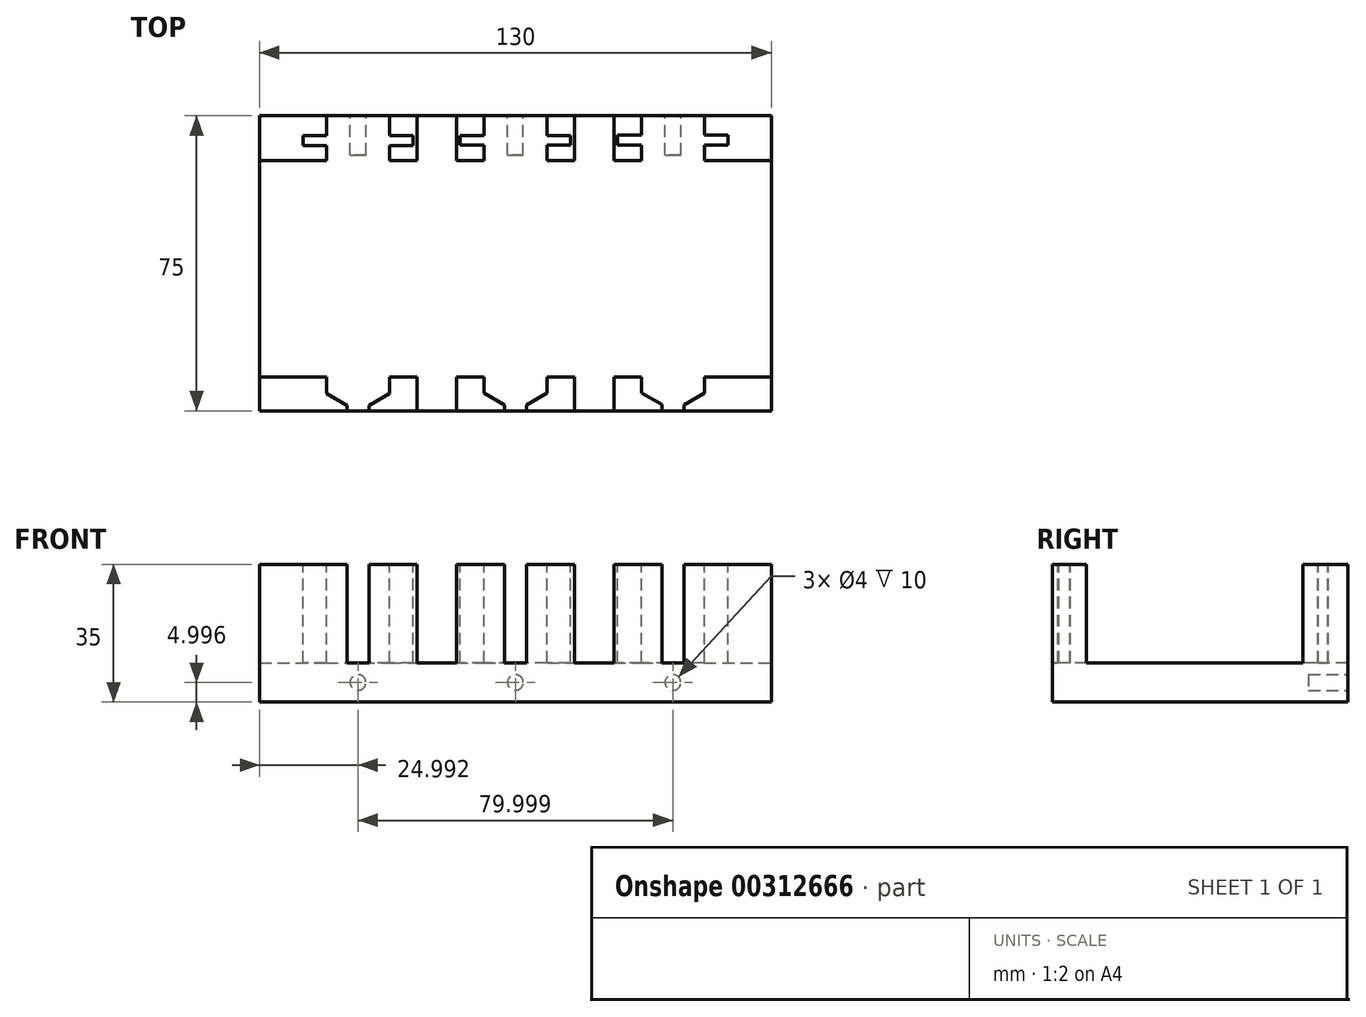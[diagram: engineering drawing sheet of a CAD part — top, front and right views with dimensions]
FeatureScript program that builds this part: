
annotation { "Feature Type Name" : "Feature", "Feature Type Description" : "" }
export const myFeature = defineFeature(function(context is Context, id is Id, definition is map)
    precondition{}
    {
        {
            var Q0;
            Q0=qCreatedBy(makeId("Front.planeOp"),FACE);
            var sketch = newSketch(context, id + "F0", { "sketchPlane" : qUnion([Q0])});
            skLineSegment(sketch, "E0.bottom", {"start": v(-64.2, 25.08) * mm, "end": v(65.8, 25.08) * mm});
            skLineSegment(sketch, "E0.top", {"start": v(-64.2, -24.92) * mm, "end": v(65.8, -24.92) * mm});
            skLineSegment(sketch, "E0.left", {"start": v(-64.2, 25.08) * mm, "end": v(-64.2, -24.92) * mm});
            skLineSegment(sketch, "E0.right", {"start": v(65.8, 25.08) * mm, "end": v(65.8, -24.92) * mm});
            skSolve(sketch);
        }
        {
            var Q0;
            Q0=makeQuery(id+"F0.imprint","IMPRINT",FACE,{"disambiguationData":[TD([[makeQuery(id+"F0.imprint","IMPRINT",EDGE,{"derivedFrom":sQuery(id+"F0.wireOp",EDGE,"E0.bottom")}),-1.0]])]});
            extrude(context, id + "F1", {"entities" : qUnion([Q0]), "depth" : 150 * mm});
        }
        {
            var Q0;
            Q0=makeQuery(id+"F1.opExtrude","SWEPT_FACE",FACE,{"disambiguationData":[OSD([sQuery(id+"F0.wireOp",EDGE,"E0.right")])]});
            var sketch = newSketch(context, id + "F2", { "sketchPlane" : qUnion([Q0])});
            skLineSegment(sketch, "E1.bottom", {"start": v(-75, 25.08) * mm, "end": v(0, 25.08) * mm});
            skLineSegment(sketch, "E1.top", {"start": v(-75, 0) * mm, "end": v(0, 0) * mm});
            skLineSegment(sketch, "E1.left", {"start": v(-75, 25.08) * mm, "end": v(-75, 0) * mm});
            skLineSegment(sketch, "E1.right", {"start": v(0, 25.08) * mm, "end": v(0, 0) * mm});
            skSolve(sketch);
        }
        {
            var Q0;
            Q0=makeQuery(id+"F2.imprint","IMPRINT",FACE,{"disambiguationData":[TD([[makeQuery(id+"F2.imprint","IMPRINT",EDGE,{"derivedFrom":sQuery(id+"F2.wireOp",EDGE,"E1.bottom")}),-1.0]])]});
            extrude(context, id + "F3", {"entities" : qUnion([Q0]), "operationType" : NewBodyOperationType.REMOVE, "endBound" : BoundingType.THROUGH_ALL, "oppositeDirection" : true, "depth" : 160 * mm});
        }
        {
            var Q0;
            Q0=makeQuery(id+"F1.opExtrude","SWEPT_FACE",FACE,{"disambiguationData":[OSD([sQuery(id+"F0.wireOp",EDGE,"E0.bottom")])]});
            var sketch = newSketch(context, id + "F4", { "sketchPlane" : qUnion([Q0])});
            skPoint(sketch, "E2", {"position": v(-54.2, -75) * mm});
            skPoint(sketch, "E3", {"position": v(-24.2, -75) * mm});
            skPoint(sketch, "E4", {"position": v(-64.2, -75) * mm});
            skPoint(sketch, "E5", {"position": v(-14.2, -75) * mm});
            skPoint(sketch, "E6", {"position": v(15.8, -75) * mm});
            skPoint(sketch, "E7", {"position": v(25.8, -75) * mm});
            skPoint(sketch, "E8", {"position": v(55.8, -75) * mm});
            skLineSegment(sketch, "E9", {"start": v(-24.2, -75) * mm, "end": v(-24.2, -150) * mm, "construction": true});
            skLineSegment(sketch, "E10", {"start": v(-14.2, -75) * mm, "end": v(-14.2, -150) * mm, "construction": true});
            skLineSegment(sketch, "E11", {"start": v(15.8, -75) * mm, "end": v(15.8, -150) * mm, "construction": true});
            skLineSegment(sketch, "E12", {"start": v(25.8, -75) * mm, "end": v(25.8, -150) * mm, "construction": true});
            skLineSegment(sketch, "E13", {"start": v(55.8, -75) * mm, "end": v(55.8, -150) * mm, "construction": true});
            skLineSegment(sketch, "E14.bottom", {"start": v(-24.2, -75) * mm, "end": v(-14.2, -75) * mm});
            skLineSegment(sketch, "E14.top", {"start": v(-24.2, -150) * mm, "end": v(-14.2, -150) * mm});
            skLineSegment(sketch, "E14.left", {"start": v(-24.2, -75) * mm, "end": v(-24.2, -150) * mm});
            skLineSegment(sketch, "E14.right", {"start": v(-14.2, -75) * mm, "end": v(-14.2, -150) * mm});
            skLineSegment(sketch, "E15.bottom", {"start": v(15.8, -75) * mm, "end": v(25.8, -75) * mm});
            skLineSegment(sketch, "E15.top", {"start": v(15.8, -150) * mm, "end": v(25.8, -150) * mm});
            skLineSegment(sketch, "E15.left", {"start": v(15.8, -75) * mm, "end": v(15.8, -150) * mm});
            skLineSegment(sketch, "E15.right", {"start": v(25.8, -75) * mm, "end": v(25.8, -150) * mm});
            skLineSegment(sketch, "E16", {"start": v(-54.2, -75) * mm, "end": v(-54.2, -150) * mm, "construction": true});
            skSolve(sketch);
        }
        {
            var Q0;
            {var subQ0=sQuery(id+"F0.wireOp",EDGE,"E0.bottom");Q0=makeQuery(id+"F4.imprint","IMPRINT",FACE,{"disambiguationData":[TD([[makeQuery(id+"F4.imprint","IMPRINT",EDGE,{"derivedFrom":makeQuery(id+"F1.opExtrude","CAP_EDGE",EDGE,{"disambiguationData":[OSD([subQ0])],"isStart":false})}),1.0]])]});}
            var sketch = newSketch(context, id + "F5", { "sketchPlane" : qUnion([Q0])});
            skPoint(sketch, "E17", {"position": v(-64.2, -74.98) * mm});
            skPoint(sketch, "E18", {"position": v(-47.2, -73.6) * mm});
            skPoint(sketch, "E19", {"position": v(-31.2, -73.6) * mm});
            skLineSegment(sketch, "E20", {"start": v(-47.2, -73.6) * mm, "end": v(-47.2, -80.08) * mm});
            skLineSegment(sketch, "E21", {"start": v(-31.2, -73.6) * mm, "end": v(-31.2, -80.08) * mm});
            skLineSegment(sketch, "E22", {"start": v(-47.2, -80.08) * mm, "end": v(-53.22, -80.08) * mm});
            skLineSegment(sketch, "E23", {"start": v(-53.22, -80.08) * mm, "end": v(-53.22, -82.58) * mm});
            skLineSegment(sketch, "E24", {"start": v(-53.22, -82.58) * mm, "end": v(-47.2, -82.58) * mm});
            skLineSegment(sketch, "E25", {"start": v(-31.2, -80.08) * mm, "end": v(-25.26, -80.08) * mm});
            skLineSegment(sketch, "E26", {"start": v(-25.26, -80.08) * mm, "end": v(-25.26, -82.58) * mm});
            skLineSegment(sketch, "E27", {"start": v(-25.26, -82.58) * mm, "end": v(-31.2, -82.58) * mm});
            skLineSegment(sketch, "E28", {"start": v(-47.2, -82.58) * mm, "end": v(-47.2, -145.58) * mm});
            skLineSegment(sketch, "E29", {"start": v(-31.2, -82.58) * mm, "end": v(-31.2, -145.58) * mm});
            skLineSegment(sketch, "E30", {"start": v(-47.2, -145.58) * mm, "end": v(-42.01, -148.58) * mm});
            skLineSegment(sketch, "E31", {"start": v(-31.2, -145.58) * mm, "end": v(-36.4, -148.58) * mm});
            skLineSegment(sketch, "E32", {"start": v(-47.2, -73.6) * mm, "end": v(-31.2, -73.6) * mm});
            skLineSegment(sketch, "E33", {"start": v(-42.01, -148.58) * mm, "end": v(-42.01, -151.87) * mm});
            skLineSegment(sketch, "E34", {"start": v(-42.01, -151.87) * mm, "end": v(-36.48, -151.88) * mm});
            skLineSegment(sketch, "E35", {"start": v(-36.48, -151.88) * mm, "end": v(-36.4, -148.58) * mm});
            skSolve(sketch);
        }
        {
            var Q0;
            {var subQ1=sQuery(id+"F5.wireOp",EDGE,"E22");Q0=makeQuery(id+"F5.imprint","IMPRINT",FACE,{"disambiguationData":[TD([[makeQuery(id+"F5.imprint","IMPRINT",EDGE,{"derivedFrom":subQ1}),1.0]])]});}
            extrude(context, id + "F6", {"entities" : qUnion([Q0]), "operationType" : NewBodyOperationType.REMOVE, "oppositeDirection" : true, "depth" : 25 * mm});
        }
        {
            var Q0;
            {var subQ0=sQuery(id+"F0.wireOp",EDGE,"E0.bottom");Q0=makeQuery(id+"F4.imprint","IMPRINT",FACE,{"disambiguationData":[TD([[makeQuery(id+"F4.imprint","IMPRINT",EDGE,{"derivedFrom":makeQuery(id+"F1.opExtrude","CAP_EDGE",EDGE,{"disambiguationData":[OSD([subQ0])],"isStart":false})}),1.0]])]});}
            var sketch = newSketch(context, id + "F7", { "sketchPlane" : qUnion([Q0])});
            skPoint(sketch, "E36", {"position": v(48.8, -73.93) * mm});
            skPoint(sketch, "E37", {"position": v(32.8, -73.87) * mm});
            skLineSegment(sketch, "E38", {"start": v(32.8, -73.87) * mm, "end": v(32.8, -79.9) * mm});
            skLineSegment(sketch, "E39", {"start": v(32.8, -79.9) * mm, "end": v(26.8, -79.9) * mm});
            skLineSegment(sketch, "E40", {"start": v(26.8, -82.4) * mm, "end": v(26.8, -79.9) * mm});
            skLineSegment(sketch, "E41", {"start": v(26.8, -82.4) * mm, "end": v(32.8, -82.4) * mm});
            skLineSegment(sketch, "E42", {"start": v(32.8, -82.4) * mm, "end": v(32.8, -145.4) * mm});
            skLineSegment(sketch, "E43", {"start": v(48.8, -73.93) * mm, "end": v(48.8, -79.98) * mm});
            skLineSegment(sketch, "E44", {"start": v(48.8, -79.98) * mm, "end": v(54.8, -79.98) * mm});
            skLineSegment(sketch, "E45", {"start": v(54.8, -79.98) * mm, "end": v(54.8, -82.48) * mm});
            skLineSegment(sketch, "E46", {"start": v(48.8, -82.48) * mm, "end": v(54.8, -82.48) * mm});
            skLineSegment(sketch, "E47", {"start": v(48.8, -82.48) * mm, "end": v(48.8, -145.48) * mm});
            skLineSegment(sketch, "E48", {"start": v(32.8, -73.87) * mm, "end": v(48.8, -73.93) * mm});
            skLineSegment(sketch, "E49", {"start": v(32.8, -145.4) * mm, "end": v(37.99, -148.4) * mm});
            skLineSegment(sketch, "E50", {"start": v(37.99, -148.4) * mm, "end": v(37.99, -152.65) * mm});
            skLineSegment(sketch, "E51", {"start": v(48.8, -145.48) * mm, "end": v(43.6, -148.48) * mm});
            skLineSegment(sketch, "E52", {"start": v(43.6, -148.48) * mm, "end": v(43.6, -152.65) * mm});
            skLineSegment(sketch, "E53", {"start": v(37.99, -152.65) * mm, "end": v(43.6, -152.65) * mm});
            skSolve(sketch);
        }
        {
            var Q0;
            Q0 = qSketchRegion(id + "F7", true);
            extrude(context, id + "F8", {"entities" : qUnion([Q0]), "operationType" : NewBodyOperationType.REMOVE, "oppositeDirection" : true, "depth" : 25 * mm});
        }
        {
            var Q0;
            {var subQ0=sQuery(id+"F0.wireOp",EDGE,"E0.bottom");Q0=makeQuery(id+"F4.imprint","IMPRINT",FACE,{"disambiguationData":[TD([[makeQuery(id+"F4.imprint","IMPRINT",EDGE,{"derivedFrom":makeQuery(id+"F1.opExtrude","CAP_EDGE",EDGE,{"disambiguationData":[OSD([subQ0])],"isStart":false})}),1.0]])]});}
            var sketch = newSketch(context, id + "F9", { "sketchPlane" : qUnion([Q0])});
            skPoint(sketch, "E54", {"position": v(-7.22, -73.73) * mm});
            skLineSegment(sketch, "E55", {"start": v(-7.22, -73.73) * mm, "end": v(8.78, -73.73) * mm});
            skLineSegment(sketch, "E56", {"start": v(-7.22, -73.73) * mm, "end": v(-7.22, -80) * mm});
            skLineSegment(sketch, "E57", {"start": v(-7.22, -80) * mm, "end": v(-13.22, -80) * mm});
            skLineSegment(sketch, "E58", {"start": v(-13.22, -80) * mm, "end": v(-13.22, -82.5) * mm});
            skLineSegment(sketch, "E59", {"start": v(-13.22, -82.5) * mm, "end": v(-7.22, -82.5) * mm});
            skLineSegment(sketch, "E60", {"start": v(-7.22, -82.5) * mm, "end": v(-7.22, -145.5) * mm});
            skLineSegment(sketch, "E61", {"start": v(-7.22, -145.5) * mm, "end": v(-2.03, -148.5) * mm});
            skLineSegment(sketch, "E62", {"start": v(8.78, -73.73) * mm, "end": v(8.78, -80) * mm});
            skLineSegment(sketch, "E63", {"start": v(8.78, -80) * mm, "end": v(14.78, -80) * mm});
            skLineSegment(sketch, "E64", {"start": v(14.78, -80) * mm, "end": v(14.78, -82.5) * mm});
            skLineSegment(sketch, "E65", {"start": v(14.78, -82.5) * mm, "end": v(8.78, -82.5) * mm});
            skLineSegment(sketch, "E66", {"start": v(8.78, -82.5) * mm, "end": v(8.78, -145.5) * mm});
            skLineSegment(sketch, "E67", {"start": v(8.78, -145.5) * mm, "end": v(3.58, -148.5) * mm});
            skLineSegment(sketch, "E68", {"start": v(-2.03, -148.5) * mm, "end": v(-2.03, -153.14) * mm});
            skLineSegment(sketch, "E69", {"start": v(-2.03, -153.14) * mm, "end": v(3.63, -153.14) * mm});
            skLineSegment(sketch, "E70", {"start": v(3.63, -153.14) * mm, "end": v(3.58, -148.5) * mm});
            skSolve(sketch);
        }
        {
            var Q0;
            Q0 = qSketchRegion(id + "F9", true);
            extrude(context, id + "F10", {"entities" : qUnion([Q0]), "operationType" : NewBodyOperationType.REMOVE, "oppositeDirection" : true, "depth" : 25 * mm});
        }
        {
            var Q0;
            Q0=makeQuery(id+"F1.opExtrude","SWEPT_FACE",FACE,{"disambiguationData":[OSD([sQuery(id+"F0.wireOp",EDGE,"E0.right")])]});
            var sketch = newSketch(context, id + "F11", { "sketchPlane" : qUnion([Q0])});
            skPoint(sketch, "E71", {"position": v(-150, -24.92) * mm});
            skPoint(sketch, "E72", {"position": v(-150, -9.92) * mm});
            skLineSegment(sketch, "E73.bottom", {"start": v(-150, -9.92) * mm, "end": v(1.85, -9.92) * mm});
            skLineSegment(sketch, "E73.top", {"start": v(-150, -24.92) * mm, "end": v(1.85, -24.92) * mm});
            skLineSegment(sketch, "E73.left", {"start": v(-150, -9.92) * mm, "end": v(-150, -24.92) * mm});
            skLineSegment(sketch, "E73.right", {"start": v(1.85, -9.92) * mm, "end": v(1.85, -24.92) * mm});
            skSolve(sketch);
        }
        {
            var Q0;
            {var subQ0=sQuery(id+"F11.wireOp",EDGE,"E73.left");Q0=makeQuery(id+"F11.imprint","IMPRINT",FACE,{"disambiguationData":[TD([[makeQuery(id+"F11.imprint","IMPRINT",EDGE,{"derivedFrom":subQ0}),1.0]])]});}
            extrude(context, id + "F12", {"entities" : qUnion([Q0]), "operationType" : NewBodyOperationType.REMOVE, "oppositeDirection" : true, "depth" : 161 * mm});
        }
        {
            var Q0;
            Q0=makeQuery(id+"F3.boolean.opBoolean","COPY",FACE,{"derivedFrom":makeQuery(id+"F3.opExtrude","SWEPT_FACE",FACE,{"disambiguationData":[OSD([sQuery(id+"F2.wireOp",EDGE,"E1.top")])]})});
            var sketch = newSketch(context, id + "F13", { "sketchPlane" : qUnion([Q0])});
            skPoint(sketch, "E74", {"position": v(-44.2, -75) * mm});
            skPoint(sketch, "E75", {"position": v(-34.2, -75) * mm});
            skPoint(sketch, "E76", {"position": v(-4.22, -75) * mm});
            skPoint(sketch, "E77", {"position": v(5.78, -75) * mm});
            skPoint(sketch, "E78", {"position": v(35.8, -75) * mm});
            skPoint(sketch, "E79", {"position": v(45.81, -75) * mm});
            skLineSegment(sketch, "E80.bottom", {"start": v(-44.2, -75) * mm, "end": v(-64.2, -75) * mm});
            skLineSegment(sketch, "E80.top", {"start": v(-44.2, 0) * mm, "end": v(-64.2, 0) * mm});
            skLineSegment(sketch, "E80.left", {"start": v(-44.2, -75) * mm, "end": v(-44.2, 0) * mm});
            skLineSegment(sketch, "E80.right", {"start": v(-64.2, -75) * mm, "end": v(-64.2, 0) * mm});
            skPoint(sketch, "E81.oppositeSnap0", {"position": v(-54.2, 0) * mm});
            skLineSegment(sketch, "E81.bottom", {"start": v(-34.2, -75) * mm, "end": v(-4.22, -75) * mm});
            skLineSegment(sketch, "E81.top", {"start": v(-34.2, 0) * mm, "end": v(-4.22, 0) * mm});
            skLineSegment(sketch, "E81.left", {"start": v(-34.2, -75) * mm, "end": v(-34.2, 0) * mm});
            skLineSegment(sketch, "E81.right", {"start": v(-4.22, -75) * mm, "end": v(-4.22, 0) * mm});
            skLineSegment(sketch, "E82.bottom", {"start": v(5.78, -75) * mm, "end": v(35.8, -75) * mm});
            skLineSegment(sketch, "E82.top", {"start": v(5.78, 0) * mm, "end": v(35.8, 0) * mm});
            skLineSegment(sketch, "E82.left", {"start": v(5.78, -75) * mm, "end": v(5.78, 0) * mm});
            skLineSegment(sketch, "E82.right", {"start": v(35.8, -75) * mm, "end": v(35.8, 0) * mm});
            skLineSegment(sketch, "E83.bottom", {"start": v(45.81, -75) * mm, "end": v(65.8, -75) * mm});
            skLineSegment(sketch, "E83.top", {"start": v(45.81, 0) * mm, "end": v(65.8, 0) * mm});
            skLineSegment(sketch, "E83.left", {"start": v(45.81, -75) * mm, "end": v(45.81, 0) * mm});
            skLineSegment(sketch, "E83.right", {"start": v(65.8, -75) * mm, "end": v(65.8, 0) * mm});
            skSolve(sketch);
        }
        {
            var Q0;
            Q0=makeQuery(id+"F13.imprint","IMPRINT",FACE,{"disambiguationData":[TD([[makeQuery(id+"F13.imprint","IMPRINT",EDGE,{"derivedFrom":sQuery(id+"F13.wireOp",EDGE,"E80.bottom")}),1.0]])]});
            var Q1;
            Q1=makeQuery(id+"F13.imprint","IMPRINT",FACE,{"disambiguationData":[TD([[makeQuery(id+"F13.imprint","IMPRINT",EDGE,{"derivedFrom":sQuery(id+"F13.wireOp",EDGE,"E81.bottom")}),1.0]])]});
            var Q2;
            Q2=makeQuery(id+"F13.imprint","IMPRINT",FACE,{"disambiguationData":[TD([[makeQuery(id+"F13.imprint","IMPRINT",EDGE,{"derivedFrom":sQuery(id+"F13.wireOp",EDGE,"E82.bottom")}),1.0]])]});
            var Q3;
            Q3=makeQuery(id+"F13.imprint","IMPRINT",FACE,{"disambiguationData":[TD([[makeQuery(id+"F13.imprint","IMPRINT",EDGE,{"derivedFrom":sQuery(id+"F13.wireOp",EDGE,"E83.bottom")}),1.0]])]});
            extrude(context, id + "F14", {"entities" : qUnion([Q0, Q1, Q2, Q3]), "operationType" : NewBodyOperationType.REMOVE, "oppositeDirection" : true, "depth" : 25 * mm});
        }
        {
            var Q0;
            Q0=makeQuery(id+"F14.boolean.opBoolean","COPY",FACE,{"derivedFrom":makeQuery(id+"F14.opExtrude","SWEPT_FACE",FACE,{"disambiguationData":[OSD([sQuery(id+"F13.wireOp",EDGE,"E83.left")])]})});
            var sketch = newSketch(context, id + "F15", { "sketchPlane" : qUnion([Q0])});
            skLineSegment(sketch, "E84.bottom", {"start": v(-75, 0) * mm, "end": v(0, 0) * mm});
            skLineSegment(sketch, "E84.top", {"start": v(-75, -9.92) * mm, "end": v(0, -9.92) * mm});
            skLineSegment(sketch, "E84.left", {"start": v(-75, 0) * mm, "end": v(-75, -9.92) * mm});
            skLineSegment(sketch, "E84.right", {"start": v(0, 0) * mm, "end": v(0, -9.92) * mm});
            skSolve(sketch);
        }
        {
            var Q0;
            Q0 = qSketchRegion(id + "F15", true);
            extrude(context, id + "F16", {"entities" : qUnion([Q0]), "operationType" : NewBodyOperationType.REMOVE, "oppositeDirection" : true, "depth" : 100 * mm});
        }
        {
            var Q0;
            Q0=makeQuery(id+"F16.boolean.opBoolean","MERGE",FACE,{"derivedFrom":[makeQuery(id+"F14.boolean.opBoolean","MERGE",FACE,{"derivedFrom":[makeQuery(id+"F3.boolean.opBoolean","COPY",FACE,{"derivedFrom":makeQuery(id+"F3.opExtrude","SWEPT_FACE",FACE,{"disambiguationData":[OSD([sQuery(id+"F2.wireOp",EDGE,"E1.left")])]})}),makeQuery(id+"F14.opExtrude","SWEPT_FACE",FACE,{"disambiguationData":[OSD([sQuery(id+"F13.wireOp",EDGE,"E80.bottom")])]}),makeQuery(id+"F14.opExtrude","SWEPT_FACE",FACE,{"disambiguationData":[OSD([sQuery(id+"F13.wireOp",EDGE,"E81.bottom")])]}),makeQuery(id+"F14.opExtrude","SWEPT_FACE",FACE,{"disambiguationData":[OSD([sQuery(id+"F13.wireOp",EDGE,"E82.bottom")])]}),makeQuery(id+"F14.opExtrude","SWEPT_FACE",FACE,{"disambiguationData":[OSD([sQuery(id+"F13.wireOp",EDGE,"E83.bottom")])]})]}),makeQuery(id+"F16.opExtrude","SWEPT_FACE",FACE,{"disambiguationData":[OSD([sQuery(id+"F15.wireOp",EDGE,"E84.left")])]})]});
            var sketch = newSketch(context, id + "F17", { "sketchPlane" : qUnion([Q0])});
            skPoint(sketch, "E85", {"position": v(-40.8, -4.92) * mm});
            skCircle(sketch, "E86", {"center": v(-40.8, -4.92) * mm, "radius": 2 * mm});
            skPoint(sketch, "E87", {"position": v(-0.78, -4.92) * mm});
            skCircle(sketch, "E88", {"center": v(-0.78, -4.92) * mm, "radius": 2 * mm});
            skPoint(sketch, "E89", {"position": v(39.2, -4.92) * mm});
            skCircle(sketch, "E90", {"center": v(39.2, -4.92) * mm, "radius": 2 * mm});
            skPoint(sketch, "E91", {"position": v(-40.8, 0.08) * mm});
            skPoint(sketch, "E92", {"position": v(-40.8, -9.92) * mm});
            skPoint(sketch, "E93", {"position": v(-0.78, 0.08) * mm});
            skPoint(sketch, "E94", {"position": v(-0.78, -9.92) * mm});
            skPoint(sketch, "E95", {"position": v(39.2, -9.92) * mm});
            skSolve(sketch);
        }
        {
            var Q0;
            Q0=makeQuery(id+"F17.imprint","IMPRINT",FACE,{"disambiguationData":[TD([[makeQuery(id+"F17.imprint","IMPRINT",EDGE,{"derivedFrom":sQuery(id+"F17.wireOp",EDGE,"E86")}),1.0]])]});
            var Q1;
            Q1=makeQuery(id+"F17.imprint","IMPRINT",FACE,{"disambiguationData":[TD([[makeQuery(id+"F17.imprint","IMPRINT",EDGE,{"derivedFrom":sQuery(id+"F17.wireOp",EDGE,"E88")}),1.0]])]});
            var Q2;
            Q2=makeQuery(id+"F17.imprint","IMPRINT",FACE,{"disambiguationData":[TD([[makeQuery(id+"F17.imprint","IMPRINT",EDGE,{"derivedFrom":sQuery(id+"F17.wireOp",EDGE,"E90")}),1.0]])]});
            extrude(context, id + "F18", {"entities" : qUnion([Q0, Q1, Q2]), "operationType" : NewBodyOperationType.REMOVE, "oppositeDirection" : true, "depth" : 10 * mm});
        }
        {
            var Q0;
            Q0=makeQuery(id+"F1.opExtrude","SWEPT_FACE",FACE,{"disambiguationData":[OSD([sQuery(id+"F0.wireOp",EDGE,"E0.right")])]});
            var sketch = newSketch(context, id + "F19", { "sketchPlane" : qUnion([Q0])});
            skPoint(sketch, "E96", {"position": v(-113.85, 25.08) * mm});
            skPoint(sketch, "E97", {"position": v(-141.35, 25.08) * mm});
            skLineSegment(sketch, "E98.bottom", {"start": v(-141.35, 25.08) * mm, "end": v(-86.35, 25.08) * mm});
            skLineSegment(sketch, "E98.top", {"start": v(-141.35, 0.08) * mm, "end": v(-86.35, 0.08) * mm});
            skLineSegment(sketch, "E98.left", {"start": v(-141.35, 25.08) * mm, "end": v(-141.35, 0.08) * mm});
            skLineSegment(sketch, "E98.right", {"start": v(-86.35, 25.08) * mm, "end": v(-86.35, 0.08) * mm});
            skSolve(sketch);
        }
        {
            var Q0;
            Q0=makeQuery(id+"F19.imprint","IMPRINT",FACE,{"disambiguationData":[TD([[makeQuery(id+"F19.imprint","IMPRINT",EDGE,{"derivedFrom":sQuery(id+"F19.wireOp",EDGE,"E98.bottom")}),-1.0]])]});
            extrude(context, id + "F20", {"entities" : qUnion([Q0]), "operationType" : NewBodyOperationType.REMOVE, "oppositeDirection" : true, "depth" : 140 * mm});
        }
        {
            var Q0;
            Q0=makeQuery(id+"F4.imprint","IMPRINT",FACE,{"disambiguationData":[TD([[makeQuery(id+"F4.imprint","IMPRINT",EDGE,{"derivedFrom":sQuery(id+"F4.wireOp",EDGE,"E14.bottom")}),-1.0]])]});
            var Q1;
            Q1=makeQuery(id+"F4.imprint","IMPRINT",FACE,{"disambiguationData":[TD([[makeQuery(id+"F4.imprint","IMPRINT",EDGE,{"derivedFrom":sQuery(id+"F4.wireOp",EDGE,"E15.bottom")}),-1.0]])]});
            extrude(context, id + "F21", {"entities" : qUnion([Q0, Q1]), "operationType" : NewBodyOperationType.REMOVE, "oppositeDirection" : true, "depth" : 25 * mm});
        }
    });
